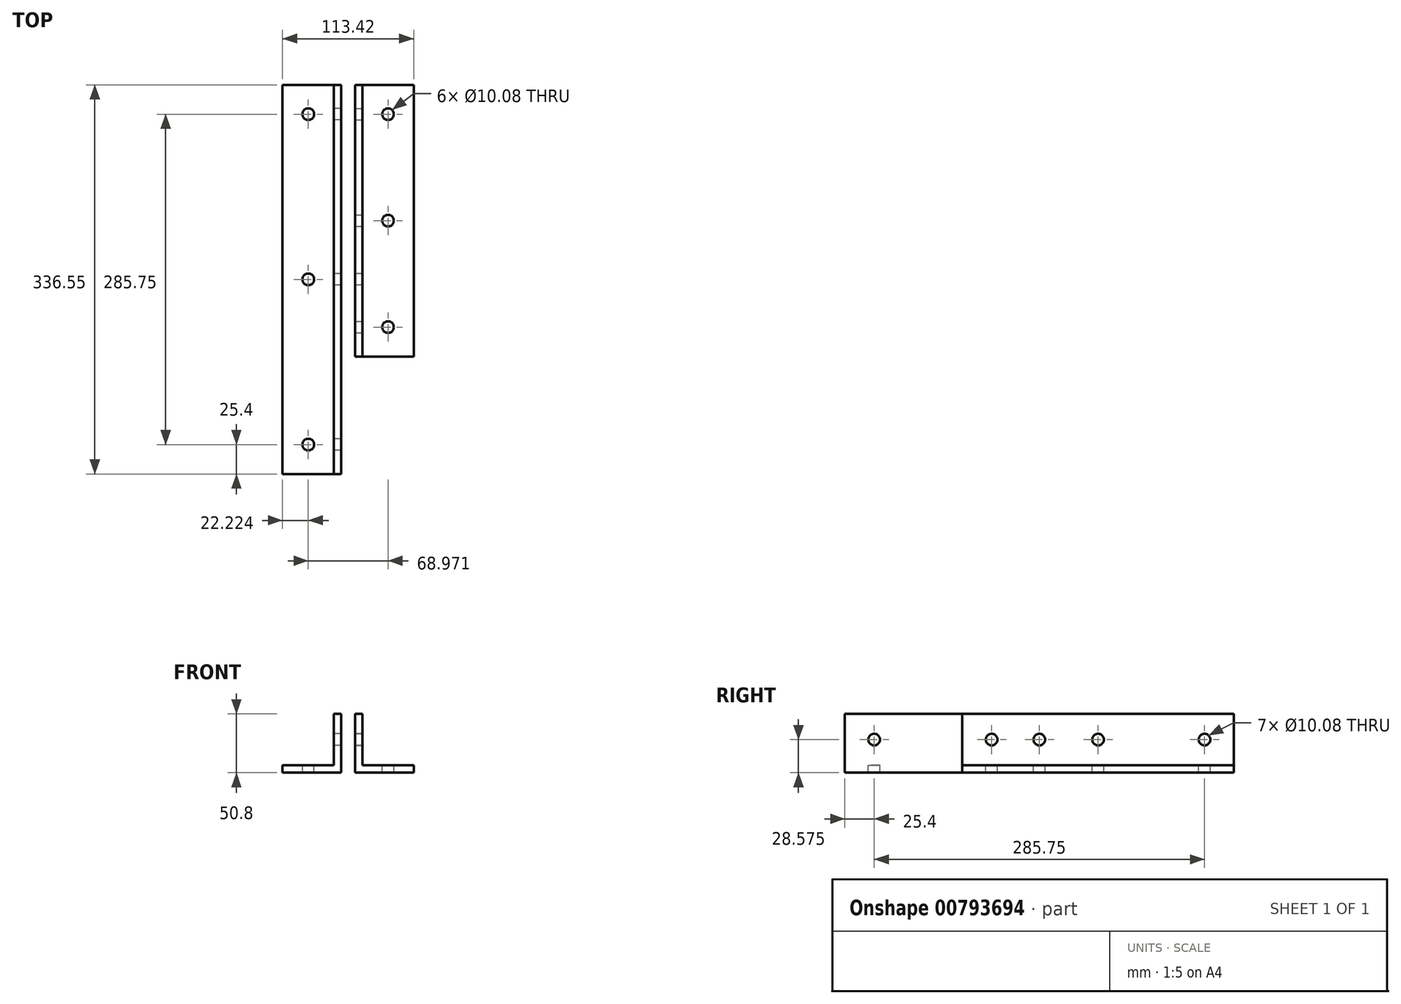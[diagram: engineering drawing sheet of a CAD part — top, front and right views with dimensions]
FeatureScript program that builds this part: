
annotation { "Feature Type Name" : "Feature", "Feature Type Description" : "" }
export const myFeature = defineFeature(function(context is Context, id is Id, definition is map)
    precondition{}
    {
        {
            var Q0;
            Q0=qCreatedBy(makeId("Front.planeOp"),FACE);
            var sketch = newSketch(context, id + "F0", { "sketchPlane" : qUnion([Q0])});
            skLineSegment(sketch, "E0", {"start": v(0, 0) * mm, "end": v(50.8, 0) * mm});
            skLineSegment(sketch, "E1", {"start": v(50.8, 0) * mm, "end": v(50.8, 6.35) * mm});
            skLineSegment(sketch, "E2", {"start": v(50.8, 6.35) * mm, "end": v(6.35, 6.35) * mm});
            skLineSegment(sketch, "E3", {"start": v(6.35, 6.35) * mm, "end": v(6.35, 50.8) * mm});
            skLineSegment(sketch, "E4", {"start": v(6.35, 50.8) * mm, "end": v(0, 50.8) * mm});
            skLineSegment(sketch, "E5", {"start": v(0, 50.8) * mm, "end": v(0, 0) * mm});
            skSolve(sketch);
        }
        {
            var Q0;
            Q0 = qSketchRegion(id + "F0", true);
            extrude(context, id + "F1", {"entities" : qUnion([Q0]), "depth" : 234.95 * mm, "offsetDistance" : 25.4 * mm});
        }
        {
            var Q0;
            Q0=makeQuery(id+"F1.opExtrude","SWEPT_FACE",FACE,{"disambiguationData":[OSD([sQuery(id+"F0.wireOp",EDGE,"E2")])]});
            var sketch = newSketch(context, id + "F2", { "sketchPlane" : qUnion([Q0])});
            skLineSegment(sketch, "E6", {"start": v(28.58, 0) * mm, "end": v(28.58, -234.95) * mm, "construction": true});
            skPoint(sketch, "E7", {"position": v(28.58, -117.48) * mm});
            skPoint(sketch, "E8", {"position": v(28.58, -25.4) * mm});
            skPoint(sketch, "E9", {"position": v(28.58, -209.55) * mm});
            skSolve(sketch);
        }
        {
            var Q0;
            Q0=makeQuery(id+"F1.opExtrude","SWEPT_FACE",FACE,{"disambiguationData":[OSD([sQuery(id+"F0.wireOp",EDGE,"E3")])]});
            var sketch = newSketch(context, id + "F3", { "sketchPlane" : qUnion([Q0])});
            skLineSegment(sketch, "E10", {"start": v(0, 28.58) * mm, "end": v(-234.95, 28.58) * mm, "construction": true});
            skPoint(sketch, "E11", {"position": v(-117.48, 28.58) * mm});
            skPoint(sketch, "E12", {"position": v(-25.4, 28.58) * mm});
            skPoint(sketch, "E13", {"position": v(-209.55, 28.57) * mm});
            skSolve(sketch);
        }
        {
            var Q0;
            Q0=sQuery(id+"F3.wireOp",VERTEX,"E12");
            var Q1;
            Q1=sQuery(id+"F3.wireOp",VERTEX,"E11");
            var Q2;
            Q2=sQuery(id+"F3.wireOp",VERTEX,"E13");
            var Q3;
            Q3=sQuery(id+"F2.wireOp",VERTEX,"E9");
            var Q4;
            Q4=sQuery(id+"F2.wireOp",VERTEX,"E8");
            var Q5;
            Q5=sQuery(id+"F2.wireOp",VERTEX,"E7");
            var Q6;
            Q6=makeQuery(id+"F1.opExtrude","SWEPT_BODY",BODY,{"disambiguationData":[OSD([sQuery(id+"F0.wireOp",EDGE,"E0"),sQuery(id+"F0.wireOp",EDGE,"E1"),sQuery(id+"F0.wireOp",EDGE,"E2"),sQuery(id+"F0.wireOp",EDGE,"E3"),sQuery(id+"F0.wireOp",EDGE,"E4"),sQuery(id+"F0.wireOp",EDGE,"E5")])]});
            hole(context, id + "F4", {"style" : HoleStyle.SIMPLE, "endStyle" : HoleEndStyle.THROUGH, "standardTappedOrClearance" : lookupTablePath({ "fit" : "Normal (ASME)", "standard" : "ANSI", "size" : "3/8", "type" : "Clearance" }), "standardBlindInLast" : lookupTablePath({ "fit" : "Free", "standard" : "ANSI", "size" : "3/8", "type" : "Clearance" }), "holeDiameter" : 10.08 * mm, "majorDiameter" : 6.35 * mm, "isTappedThrough" : true, "tappedDepth" : 12.7 * mm, "tapClearance" : 3, "locations" : qUnion([Q0, Q1, Q2, Q3, Q4, Q5]), "scope" : qUnion([Q6])});
        }
        {
            var Q0;
            Q0=qCreatedBy(makeId("Front.planeOp"),FACE);
            var sketch = newSketch(context, id + "F5", { "sketchPlane" : qUnion([Q0])});
            skLineSegment(sketch, "E14", {"start": v(-11.82, 0) * mm, "end": v(-11.82, 50.8) * mm});
            skLineSegment(sketch, "E15", {"start": v(-11.82, 50.8) * mm, "end": v(-18.17, 50.8) * mm});
            skLineSegment(sketch, "E16", {"start": v(-18.17, 50.8) * mm, "end": v(-18.17, 6.35) * mm});
            skLineSegment(sketch, "E17", {"start": v(-18.17, 6.35) * mm, "end": v(-62.62, 6.35) * mm});
            skLineSegment(sketch, "E18", {"start": v(-62.62, 6.35) * mm, "end": v(-62.62, 0) * mm});
            skLineSegment(sketch, "E19", {"start": v(-62.62, 0) * mm, "end": v(-11.82, 0) * mm});
            skSolve(sketch);
        }
        {
            var Q0;
            Q0 = qSketchRegion(id + "F5", true);
            extrude(context, id + "F6", {"entities" : qUnion([Q0]), "depth" : 336.55 * mm, "offsetDistance" : 25.4 * mm});
        }
        {
            var Q0;
            Q0=makeQuery(id+"F6.opExtrude","SWEPT_FACE",FACE,{"disambiguationData":[OSD([sQuery(id+"F5.wireOp",EDGE,"E17")])]});
            var sketch = newSketch(context, id + "F7", { "sketchPlane" : qUnion([Q0])});
            skLineSegment(sketch, "E20", {"start": v(-40.4, 0) * mm, "end": v(-40.4, -336.55) * mm, "construction": true});
            skPoint(sketch, "E21", {"position": v(-40.4, -168.28) * mm});
            skPoint(sketch, "E22", {"position": v(-40.4, -25.4) * mm});
            skPoint(sketch, "E23", {"position": v(-40.4, -311.15) * mm});
            skSolve(sketch);
        }
        {
            var Q0;
            Q0=makeQuery(id+"F6.opExtrude","SWEPT_FACE",FACE,{"disambiguationData":[OSD([sQuery(id+"F5.wireOp",EDGE,"E16")])]});
            var sketch = newSketch(context, id + "F8", { "sketchPlane" : qUnion([Q0])});
            skLineSegment(sketch, "E24", {"start": v(0, 28.58) * mm, "end": v(336.55, 28.58) * mm, "construction": true});
            skPoint(sketch, "E25", {"position": v(25.4, 28.57) * mm});
            skPoint(sketch, "E26", {"position": v(168.28, 28.58) * mm});
            skPoint(sketch, "E27", {"position": v(311.15, 28.58) * mm});
            skSolve(sketch);
        }
        {
            var Q0;
            Q0=sQuery(id+"F8.wireOp",VERTEX,"E25");
            var Q1;
            Q1=sQuery(id+"F8.wireOp",VERTEX,"E26");
            var Q2;
            Q2=sQuery(id+"F8.wireOp",VERTEX,"E27");
            var Q3;
            Q3=sQuery(id+"F7.wireOp",VERTEX,"E21");
            var Q4;
            Q4=sQuery(id+"F7.wireOp",VERTEX,"E22");
            var Q5;
            Q5=sQuery(id+"F7.wireOp",VERTEX,"E23");
            var Q6;
            Q6=makeQuery(id+"F1.opExtrude","SWEPT_BODY",BODY,{"disambiguationData":[OSD([sQuery(id+"F0.wireOp",EDGE,"E0"),sQuery(id+"F0.wireOp",EDGE,"E1"),sQuery(id+"F0.wireOp",EDGE,"E2"),sQuery(id+"F0.wireOp",EDGE,"E3"),sQuery(id+"F0.wireOp",EDGE,"E4"),sQuery(id+"F0.wireOp",EDGE,"E5")])]});
            var Q7;
            Q7=makeQuery(id+"F6.opExtrude","SWEPT_BODY",BODY,{"disambiguationData":[OSD([sQuery(id+"F5.wireOp",EDGE,"E14"),sQuery(id+"F5.wireOp",EDGE,"E15"),sQuery(id+"F5.wireOp",EDGE,"E16"),sQuery(id+"F5.wireOp",EDGE,"E17"),sQuery(id+"F5.wireOp",EDGE,"E18"),sQuery(id+"F5.wireOp",EDGE,"E19")])]});
            hole(context, id + "F9", {"style" : HoleStyle.SIMPLE, "endStyle" : HoleEndStyle.THROUGH, "standardTappedOrClearance" : lookupTablePath({ "fit" : "Normal (ASME)", "standard" : "ANSI", "size" : "3/8", "type" : "Clearance" }), "standardBlindInLast" : lookupTablePath({ "fit" : "Free", "standard" : "ANSI", "size" : "3/8", "type" : "Clearance" }), "holeDiameter" : 10.08 * mm, "majorDiameter" : 6.35 * mm, "isTappedThrough" : true, "tappedDepth" : 12.7 * mm, "tapClearance" : 3, "locations" : qUnion([Q0, Q1, Q2, Q3, Q4, Q5]), "scope" : qUnion([Q6, Q7])});
        }
    });
